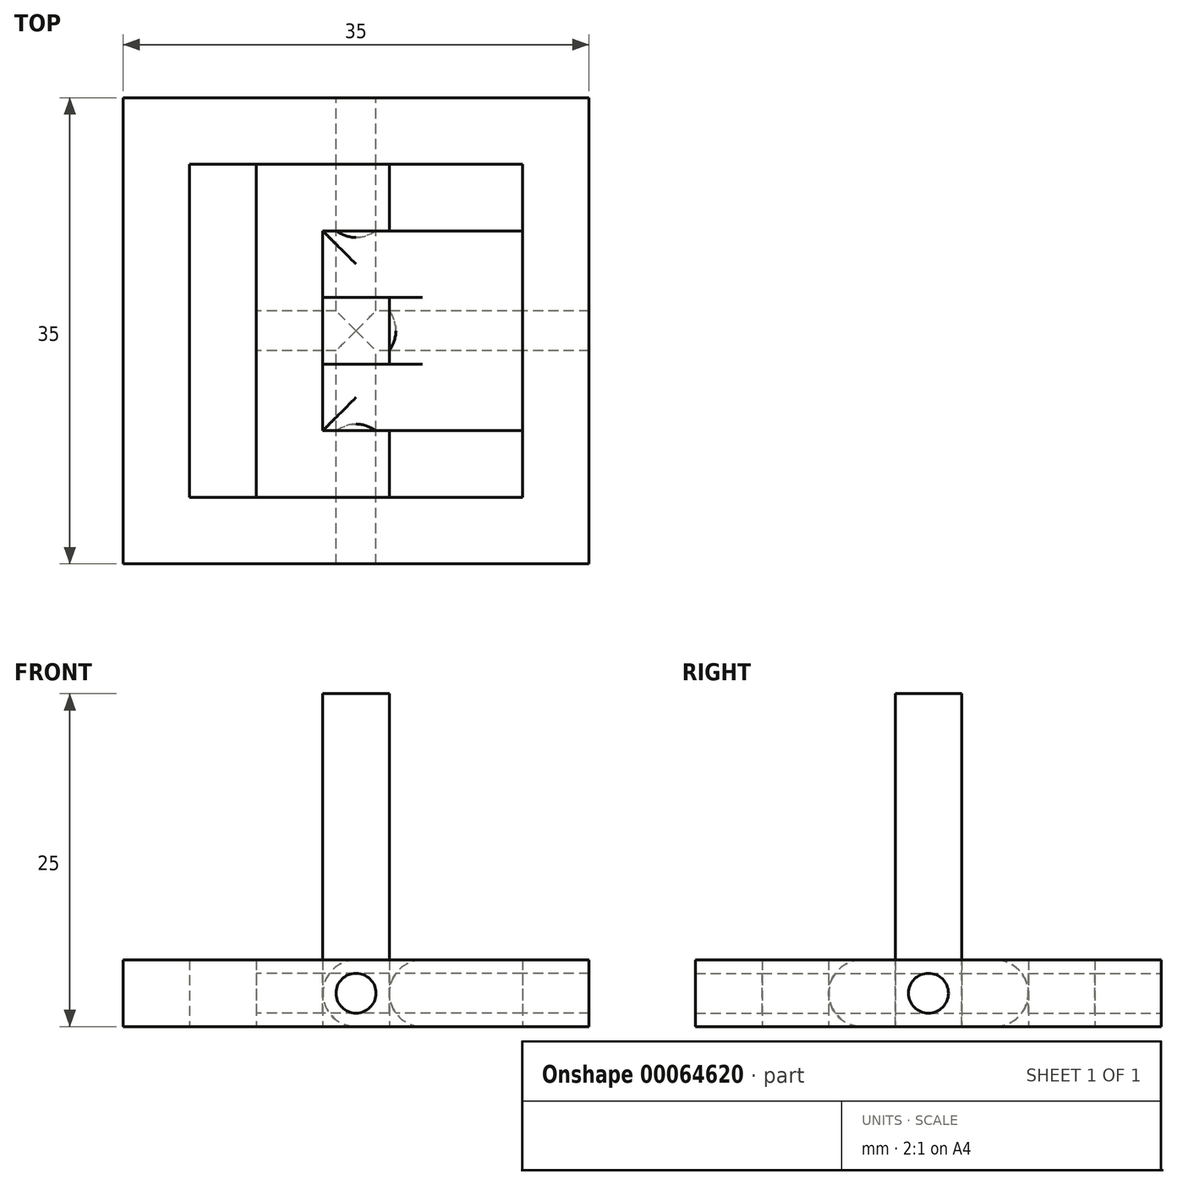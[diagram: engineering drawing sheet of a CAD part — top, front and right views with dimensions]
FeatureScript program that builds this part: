
annotation { "Feature Type Name" : "Feature", "Feature Type Description" : "" }
export const myFeature = defineFeature(function(context is Context, id is Id, definition is map)
    precondition{}
    {
        {
            var Q0;
            Q0=qCreatedBy(makeId("Top.planeOp"),FACE);
            var sketch = newSketch(context, id + "F0", { "sketchPlane" : qUnion([Q0])});
            skLineSegment(sketch, "E0.bottom", {"start": v(-2.5, 2.5) * mm, "end": v(2.5, 2.5) * mm});
            skLineSegment(sketch, "E0.top", {"start": v(-2.5, -2.5) * mm, "end": v(2.5, -2.5) * mm});
            skLineSegment(sketch, "E0.left", {"start": v(-2.5, 2.5) * mm, "end": v(-2.5, -2.5) * mm});
            skLineSegment(sketch, "E0.right", {"start": v(2.5, 2.5) * mm, "end": v(2.5, -2.5) * mm});
            skPoint(sketch, "E0.middle", {"position": v(0, 0) * mm});
            skLineSegment(sketch, "E1", {"start": v(-2.5, -2.5) * mm, "end": v(-2.5, -7.5) * mm});
            skLineSegment(sketch, "E2", {"start": v(-2.5, -7.5) * mm, "end": v(12.5, -7.5) * mm});
            skLineSegment(sketch, "E3", {"start": v(12.5, -7.5) * mm, "end": v(12.5, 7.5) * mm});
            skLineSegment(sketch, "E4", {"start": v(12.5, 7.5) * mm, "end": v(-2.5, 7.5) * mm});
            skLineSegment(sketch, "E5", {"start": v(-2.5, 7.5) * mm, "end": v(-2.5, 2.5) * mm});
            skLineSegment(sketch, "E6", {"start": v(2.5, 7.5) * mm, "end": v(2.5, 12.5) * mm});
            skLineSegment(sketch, "E7", {"start": v(2.5, 12.5) * mm, "end": v(-7.5, 12.5) * mm});
            skLineSegment(sketch, "E8", {"start": v(-7.5, 12.5) * mm, "end": v(-7.5, -12.5) * mm});
            skLineSegment(sketch, "E9", {"start": v(-7.5, -12.5) * mm, "end": v(2.5, -12.5) * mm});
            skLineSegment(sketch, "E10", {"start": v(2.5, -12.5) * mm, "end": v(2.5, -7.5) * mm});
            skSolve(sketch);
        }
        {
            var Q0;
            Q0=makeQuery(id+"F0.imprint","IMPRINT",FACE,{"disambiguationData":[TD([[makeQuery(id+"F0.imprint","IMPRINT",EDGE,{"derivedFrom":sQuery(id+"F0.wireOp",EDGE,"E0.left")}),-1.0]])]});
            extrude(context, id + "F1", {"entities" : qUnion([Q0]), "depth" : 5 * mm});
        }
        {
            var Q0;
            Q0=makeQuery(id+"F0.imprint","IMPRINT",FACE,{"disambiguationData":[TD([[makeQuery(id+"F0.imprint","IMPRINT",EDGE,{"derivedFrom":sQuery(id+"F0.wireOp",EDGE,"E0.bottom")}),1.0]])]});
            extrude(context, id + "F2", {"entities" : qUnion([Q0]), "depth" : 5 * mm});
        }
        {
            var Q0;
            Q0=makeQuery(id+"F0.imprint","IMPRINT",FACE,{"disambiguationData":[TD([[makeQuery(id+"F0.imprint","IMPRINT",EDGE,{"derivedFrom":sQuery(id+"F0.wireOp",EDGE,"E0.bottom")}),-1.0]])]});
            extrude(context, id + "F3", {"entities" : qUnion([Q0]), "depth" : 25 * mm});
        }
        {
            var Q0;
            Q0=makeQuery(id+"F2.opExtrude","CAP_EDGE",EDGE,{"disambiguationData":[OSD([sQuery(id+"F0.wireOp",EDGE,"E2")])],"isStart":false});
            var Q1;
            Q1=makeQuery(id+"F2.opExtrude","CAP_EDGE",EDGE,{"disambiguationData":[OSD([sQuery(id+"F0.wireOp",EDGE,"E2")])],"isStart":true});
            var Q2;
            Q2=makeQuery(id+"F2.opExtrude","CAP_EDGE",EDGE,{"disambiguationData":[OSD([sQuery(id+"F0.wireOp",EDGE,"E4")])],"isStart":false});
            var Q3;
            Q3=makeQuery(id+"F2.opExtrude","CAP_EDGE",EDGE,{"disambiguationData":[OSD([sQuery(id+"F0.wireOp",EDGE,"E4")])],"isStart":true});
            var Q4;
            Q4=makeQuery(id+"F2.opExtrude","CAP_EDGE",EDGE,{"disambiguationData":[OSD([sQuery(id+"F0.wireOp",EDGE,"E0.right")])],"isStart":false});
            var Q5;
            Q5=makeQuery(id+"F2.opExtrude","CAP_EDGE",EDGE,{"disambiguationData":[OSD([sQuery(id+"F0.wireOp",EDGE,"E0.right")])],"isStart":true});
            var Q6;
            Q6=makeQuery(id+"F2.opExtrude","CAP_EDGE",EDGE,{"disambiguationData":[OSD([sQuery(id+"F0.wireOp",EDGE,"E5")])],"isStart":false});
            var Q7;
            Q7=makeQuery(id+"F2.opExtrude","CAP_EDGE",EDGE,{"disambiguationData":[OSD([sQuery(id+"F0.wireOp",EDGE,"E5")])],"isStart":true});
            var Q8;
            Q8=makeQuery(id+"F2.opExtrude","CAP_EDGE",EDGE,{"disambiguationData":[OSD([sQuery(id+"F0.wireOp",EDGE,"E1")])],"isStart":true});
            var Q9;
            Q9=makeQuery(id+"F2.opExtrude","CAP_EDGE",EDGE,{"disambiguationData":[OSD([sQuery(id+"F0.wireOp",EDGE,"E1")])],"isStart":false});
            fillet(context, id + "F4", {"entities" : qUnion([Q0, Q1, Q2, Q3, Q4, Q5, Q6, Q7, Q8, Q9]), "radius" : 2.5 * mm, "tangentPropagation" : true, "allowEdgeOverflow" : false});
        }
        {
            var Q0;
            Q0=qCreatedBy(makeId("Top.planeOp"),FACE);
            var sketch = newSketch(context, id + "F5", { "sketchPlane" : qUnion([Q0])});
            skLineSegment(sketch, "E11.bottom", {"start": v(12.5, -12.5) * mm, "end": v(-12.5, -12.5) * mm});
            skLineSegment(sketch, "E11.top", {"start": v(12.5, 12.5) * mm, "end": v(-12.5, 12.5) * mm});
            skLineSegment(sketch, "E11.left", {"start": v(12.5, -12.5) * mm, "end": v(12.5, 12.5) * mm});
            skLineSegment(sketch, "E11.right", {"start": v(-12.5, -12.5) * mm, "end": v(-12.5, 12.5) * mm});
            skPoint(sketch, "E11.middle", {"position": v(0, 0) * mm});
            skLineSegment(sketch, "E12.bottom", {"start": v(17.5, -17.5) * mm, "end": v(-17.5, -17.5) * mm});
            skLineSegment(sketch, "E12.top", {"start": v(17.5, 17.5) * mm, "end": v(-17.5, 17.5) * mm});
            skLineSegment(sketch, "E12.left", {"start": v(17.5, -17.5) * mm, "end": v(17.5, 17.5) * mm});
            skLineSegment(sketch, "E12.right", {"start": v(-17.5, -17.5) * mm, "end": v(-17.5, 17.5) * mm});
            skSolve(sketch);
        }
        {
            var Q0;
            Q0 = qSketchRegion(id + "F5", true);
            extrude(context, id + "F6", {"entities" : qUnion([Q0]), "depth" : 5 * mm});
        }
        {
            var Q0;
            Q0=makeQuery(id+"F1.opExtrude","SWEPT_FACE",FACE,{"disambiguationData":[OSD([sQuery(id+"F0.wireOp",EDGE,"E8")])]});
            var sketch = newSketch(context, id + "F7", { "sketchPlane" : qUnion([Q0])});
            skCircle(sketch, "E13", {"center": v(0, 2.5) * mm, "radius": 1.5 * mm});
            skPoint(sketch, "E13.centerSnap0", {"position": v(12.5, 2.5) * mm});
            skPoint(sketch, "E13.centerSnap1", {"position": v(0, 5) * mm});
            skCircle(sketch, "E14", {"center": v(0, 2.5) * mm, "radius": 2.5 * mm});
            skSolve(sketch);
        }
        {
            var Q0;
            Q0=makeQuery(id+"F7.imprint","IMPRINT",FACE,{"disambiguationData":[TD([[makeQuery(id+"F7.imprint","IMPRINT",EDGE,{"derivedFrom":sQuery(id+"F7.wireOp",EDGE,"E13")}),1.0]])]});
            var Q1;
            Q1=makeQuery(id+"F1.opExtrude","SWEPT_BODY",BODY,{"disambiguationData":[OSD([sQuery(id+"F0.wireOp",EDGE,"E0.left"),sQuery(id+"F0.wireOp",EDGE,"E1"),sQuery(id+"F0.wireOp",EDGE,"E2"),sQuery(id+"F0.wireOp",EDGE,"E4"),sQuery(id+"F0.wireOp",EDGE,"E5"),sQuery(id+"F0.wireOp",EDGE,"E6"),sQuery(id+"F0.wireOp",EDGE,"E7"),sQuery(id+"F0.wireOp",EDGE,"E8"),sQuery(id+"F0.wireOp",EDGE,"E9"),sQuery(id+"F0.wireOp",EDGE,"E10")])]});
            extrude(context, id + "F8", {"entities" : qUnion([Q0]), "operationType" : NewBodyOperationType.REMOVE, "endBound" : BoundingType.THROUGH_ALL, "oppositeDirection" : true, "endBoundEntityBody" : qUnion([Q1]), "depth" : 25 * mm});
        }
        {
            var Q0;
            Q0=makeQuery(id+"F1.opExtrude","SWEPT_FACE",FACE,{"disambiguationData":[OSD([sQuery(id+"F0.wireOp",EDGE,"E7")])]});
            var sketch = newSketch(context, id + "F9", { "sketchPlane" : qUnion([Q0])});
            skCircle(sketch, "E15", {"center": v(0, 2.5) * mm, "radius": 1.5 * mm});
            skPoint(sketch, "E15.centerSnap0", {"position": v(-2.5, 2.5) * mm});
            skSolve(sketch);
        }
        {
            var Q0;
            Q0=makeQuery(id+"F9.imprint","IMPRINT",FACE,{"disambiguationData":[TD([[makeQuery(id+"F9.imprint","IMPRINT",EDGE,{"derivedFrom":sQuery(id+"F9.wireOp",EDGE,"E15")}),1.0]])]});
            var Q1;
            Q1=makeQuery(id+"F1.opExtrude","SWEPT_BODY",BODY,{"disambiguationData":[OSD([sQuery(id+"F0.wireOp",EDGE,"E0.left"),sQuery(id+"F0.wireOp",EDGE,"E1"),sQuery(id+"F0.wireOp",EDGE,"E2"),sQuery(id+"F0.wireOp",EDGE,"E4"),sQuery(id+"F0.wireOp",EDGE,"E5"),sQuery(id+"F0.wireOp",EDGE,"E6"),sQuery(id+"F0.wireOp",EDGE,"E7"),sQuery(id+"F0.wireOp",EDGE,"E8"),sQuery(id+"F0.wireOp",EDGE,"E9"),sQuery(id+"F0.wireOp",EDGE,"E10")])]});
            extrude(context, id + "F10", {"entities" : qUnion([Q0]), "operationType" : NewBodyOperationType.REMOVE, "endBound" : BoundingType.THROUGH_ALL, "oppositeDirection" : true, "endBoundEntityBody" : qUnion([Q1]), "depth" : 25 * mm, "hasSecondDirection" : true, "secondDirectionBound" : SecondDirectionBoundingType.THROUGH_ALL, "secondDirectionOppositeDirection" : false, "secondDirectionDepth" : 25 * mm});
        }
    });
